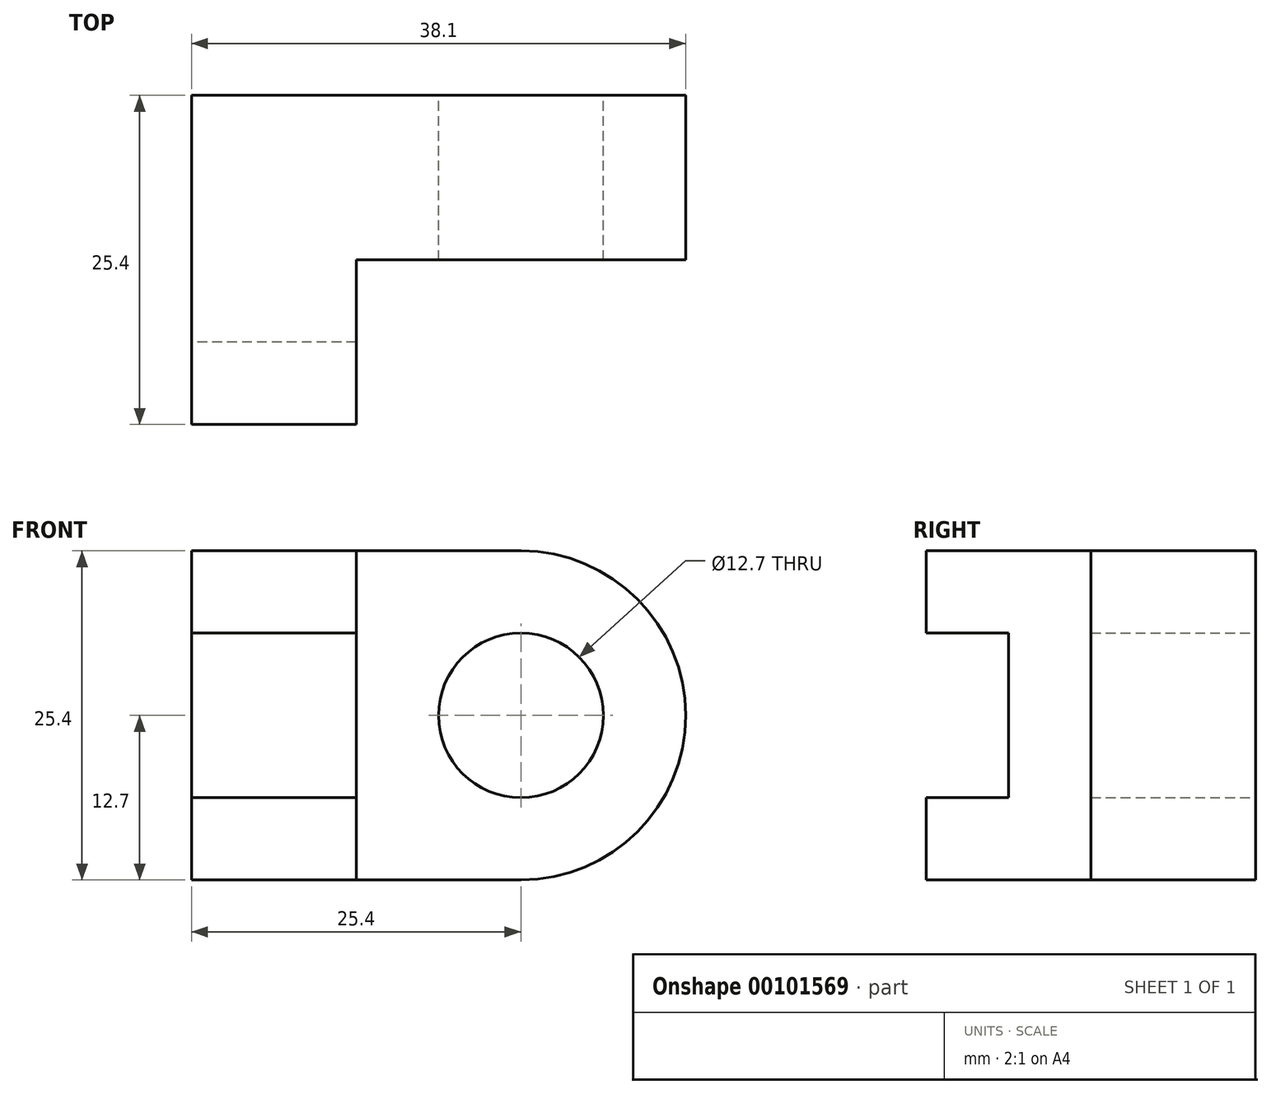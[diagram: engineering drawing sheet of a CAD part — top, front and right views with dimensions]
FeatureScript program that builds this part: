
annotation { "Feature Type Name" : "Feature", "Feature Type Description" : "" }
export const myFeature = defineFeature(function(context is Context, id is Id, definition is map)
    precondition{}
    {
        {
            var Q0;
            Q0=qCreatedBy(makeId("Top.planeOp"),FACE);
            var sketch = newSketch(context, id + "F0", { "sketchPlane" : qUnion([Q0])});
            skLineSegment(sketch, "E0", {"start": v(0, 0) * mm, "end": v(0, -25.4) * mm});
            skLineSegment(sketch, "E1", {"start": v(0, -25.4) * mm, "end": v(12.7, -25.4) * mm});
            skLineSegment(sketch, "E2", {"start": v(12.7, -25.4) * mm, "end": v(12.7, -12.7) * mm});
            skLineSegment(sketch, "E3", {"start": v(12.7, -12.7) * mm, "end": v(38.1, -12.7) * mm});
            skLineSegment(sketch, "E4", {"start": v(38.1, -12.7) * mm, "end": v(38.1, 0) * mm});
            skLineSegment(sketch, "E5", {"start": v(38.1, 0) * mm, "end": v(0, 0) * mm});
            skSolve(sketch);
        }
        {
            var Q0;
            Q0 = qSketchRegion(id + "F0", true);
            extrude(context, id + "F1", {"entities" : qUnion([Q0]), "endBound" : BoundingType.SYMMETRIC, "depth" : 25.4 * mm});
        }
        {
            var Q0;
            Q0=qCreatedBy(makeId("Right.planeOp"),FACE);
            var sketch = newSketch(context, id + "F2", { "sketchPlane" : qUnion([Q0])});
            skLineSegment(sketch, "E6.bottom", {"start": v(-25.4, 6.35) * mm, "end": v(-19.05, 6.35) * mm});
            skLineSegment(sketch, "E6.top", {"start": v(-25.4, -6.35) * mm, "end": v(-19.05, -6.35) * mm});
            skLineSegment(sketch, "E6.left", {"start": v(-25.4, 6.35) * mm, "end": v(-25.4, -6.35) * mm});
            skLineSegment(sketch, "E6.right", {"start": v(-19.05, 6.35) * mm, "end": v(-19.05, -6.35) * mm});
            skLineSegment(sketch, "E7", {"start": v(0, 0) * mm, "end": v(-25.4, 0) * mm, "construction": true});
            skSolve(sketch);
        }
        {
            var Q0;
            Q0 = qSketchRegion(id + "F2", true);
            extrude(context, id + "F3", {"entities" : qUnion([Q0]), "operationType" : NewBodyOperationType.REMOVE, "endBound" : BoundingType.THROUGH_ALL, "depth" : 25.4 * mm});
        }
        {
            var Q0;
            Q0=qCreatedBy(makeId("Front.planeOp"),FACE);
            var sketch = newSketch(context, id + "F4", { "sketchPlane" : qUnion([Q0])});
            skPoint(sketch, "E8", {"position": v(25.4, 0) * mm});
            skCircle(sketch, "E9", {"center": v(25.4, 0) * mm, "radius": 6.35 * mm});
            skSolve(sketch);
        }
        {
            var Q0;
            Q0 = qSketchRegion(id + "F4", true);
            extrude(context, id + "F5", {"entities" : qUnion([Q0]), "operationType" : NewBodyOperationType.REMOVE, "endBound" : BoundingType.THROUGH_ALL, "depth" : 25.4 * mm});
        }
        {
            var Q0;
            Q0=makeQuery(id+"F1.opExtrude","CAP_EDGE",EDGE,{"disambiguationData":[OSD([sQuery(id+"F0.wireOp",EDGE,"E4")])],"isStart":false});
            var Q1;
            Q1=makeQuery(id+"F1.opExtrude","CAP_EDGE",EDGE,{"disambiguationData":[OSD([sQuery(id+"F0.wireOp",EDGE,"E4")])],"isStart":true});
            fillet(context, id + "F6", {"entities" : qUnion([Q0, Q1]), "radius" : 12.7 * mm, "tangentPropagation" : true, "allowEdgeOverflow" : false});
        }
    });
